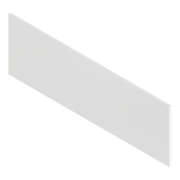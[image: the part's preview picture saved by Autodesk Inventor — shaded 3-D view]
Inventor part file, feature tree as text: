
AUTODESK INVENTOR PART (.ipt)
format: ipt  version: 2022.5 (Build 265521000, 521)  size: 77,824 bytes
history: native  units: mm
features: extrude x1, sketch x1
ambient origin geometry x8: Origin, YZ Plane, XZ Plane, XY Plane, X Axis, Y Axis, Z Axis, Center Point
bodies: Volumenkörper1 (feature_tree)
feature tree (2):
  extrude  "Extrusion1"  TaperAngle=0.0deg  [1 undecoded]
  sketch  "Skizze1"  dims[d0=74.0mm d1=0.0mm d2=24.0mm d3=1.0mm d4=0.0mm]
note: 1 required parameter value undecoded (feature->parameter linkage not recoverable at this tier; creation-order binding heuristic only, values carry confidence <= 0.55)
